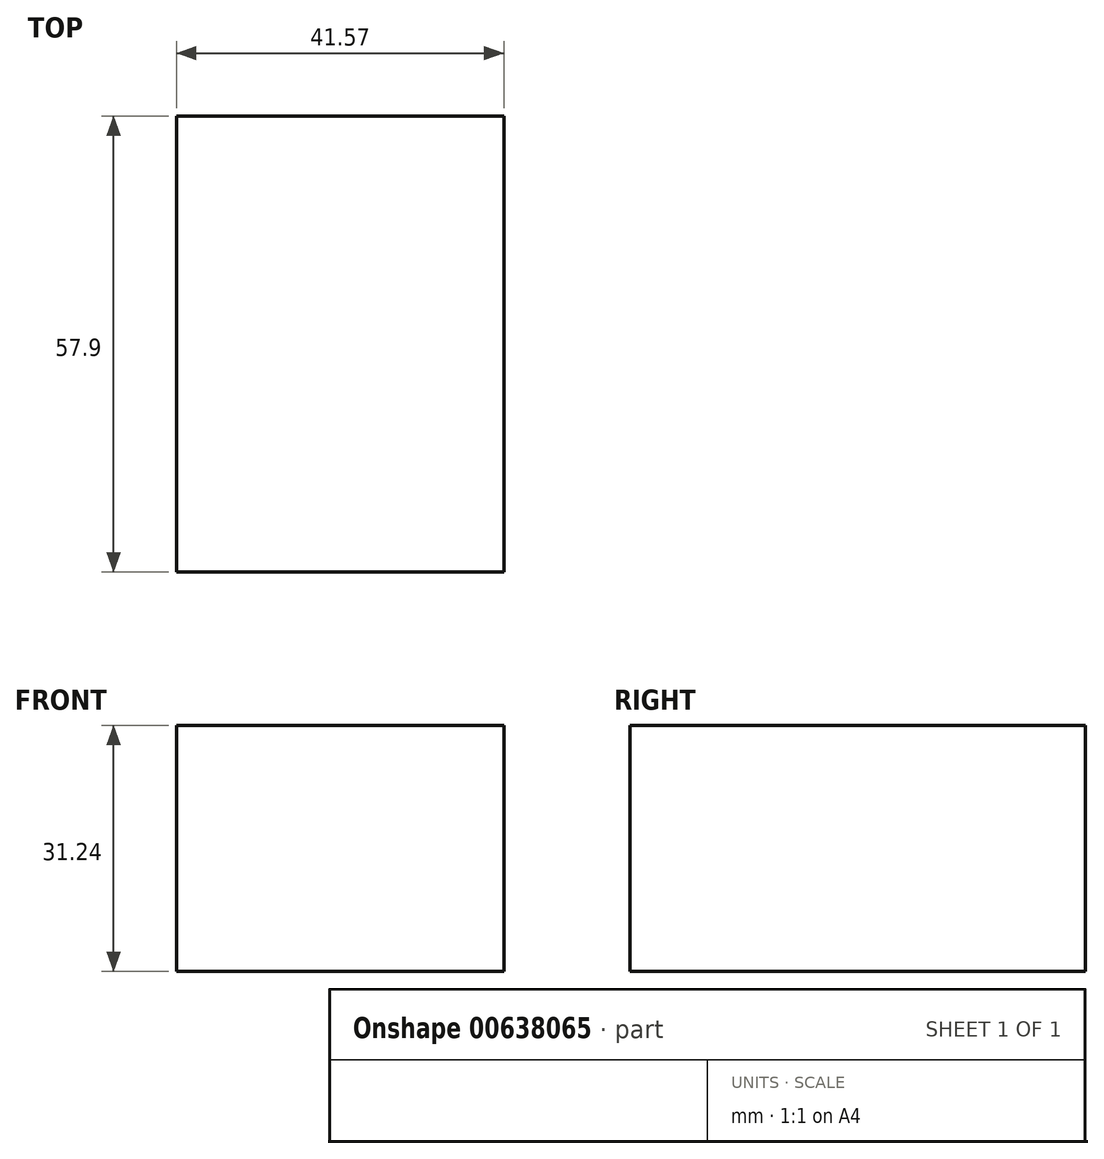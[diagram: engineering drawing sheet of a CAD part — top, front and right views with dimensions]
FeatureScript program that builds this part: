
annotation { "Feature Type Name" : "Feature", "Feature Type Description" : "" }
export const myFeature = defineFeature(function(context is Context, id is Id, definition is map)
    precondition{}
    {
        {
            var Q0;
            Q0=qCreatedBy(makeId("Top.planeOp"),FACE);
            var sketch = newSketch(context, id + "F0", { "sketchPlane" : qUnion([Q0])});
            skLineSegment(sketch, "E0.bottom", {"start": v(41.57, -57.9) * mm, "end": v(0, -57.9) * mm});
            skLineSegment(sketch, "E0.top", {"start": v(41.57, 0) * mm, "end": v(0, 0) * mm});
            skLineSegment(sketch, "E0.left", {"start": v(41.57, -57.9) * mm, "end": v(41.57, 0) * mm});
            skLineSegment(sketch, "E0.right", {"start": v(0, -57.9) * mm, "end": v(0, 0) * mm});
            skSolve(sketch);
        }
        {
            var Q0;
            Q0 = qSketchRegion(id + "F0", true);
            extrude(context, id + "F1", {"entities" : qUnion([Q0]), "depth" : 31.24 * mm, "offsetDistance" : 25.4 * mm});
        }
    });
